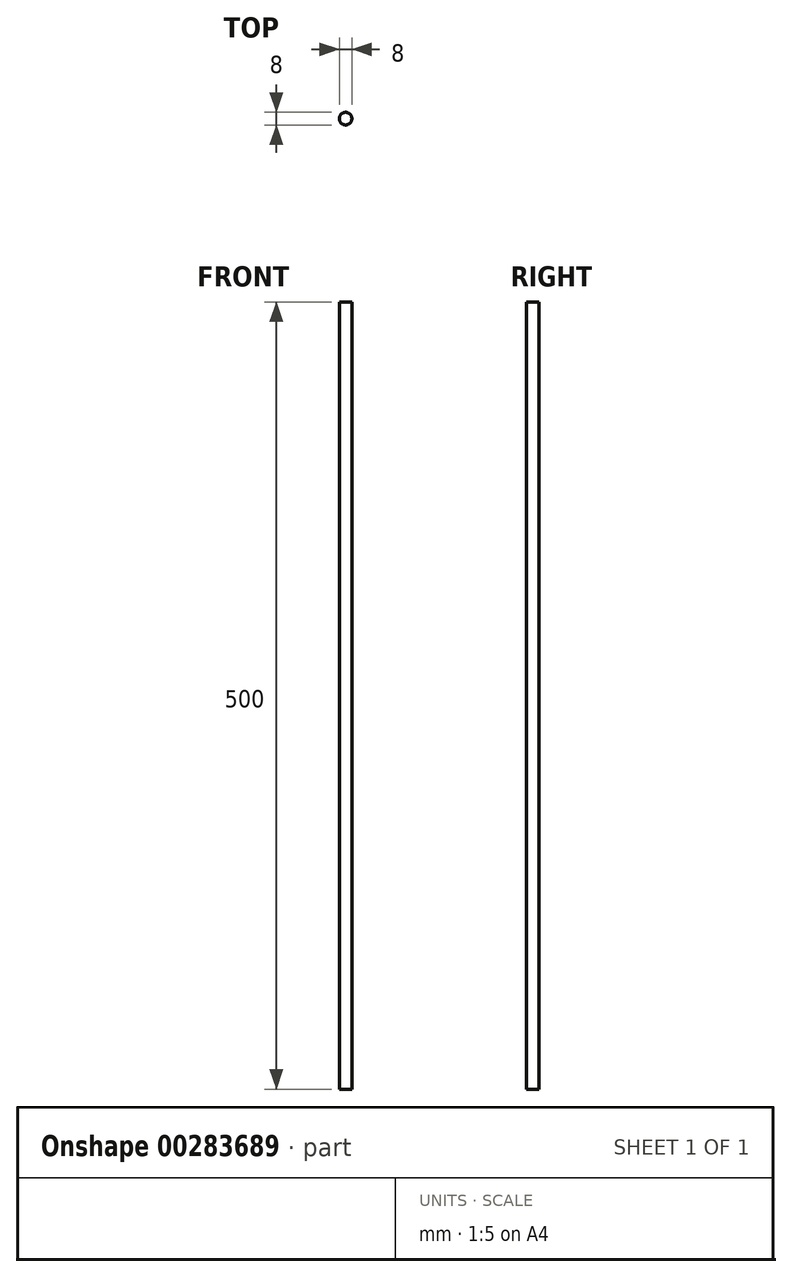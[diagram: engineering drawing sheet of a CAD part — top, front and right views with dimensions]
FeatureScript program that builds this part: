
annotation { "Feature Type Name" : "Feature", "Feature Type Description" : "" }
export const myFeature = defineFeature(function(context is Context, id is Id, definition is map)
    precondition{}
    {
        {
            var Q0;
            Q0=qCreatedBy(makeId("Top.planeOp"),FACE);
            var sketch = newSketch(context, id + "F0", { "sketchPlane" : qUnion([Q0])});
            skCircle(sketch, "E0", {"center": v(0, 0) * mm, "radius": 4 * mm});
            skSolve(sketch);
        }
        {
            var Q0;
            Q0=makeQuery(id+"F0.imprint","IMPRINT",FACE,{"disambiguationData":[TD([[makeQuery(id+"F0.imprint","IMPRINT",EDGE,{"derivedFrom":sQuery(id+"F0.wireOp",EDGE,"E0")}),1.0]])]});
            extrude(context, id + "F1", {"entities" : qUnion([Q0]), "depth" : 500 * mm});
        }
    });
